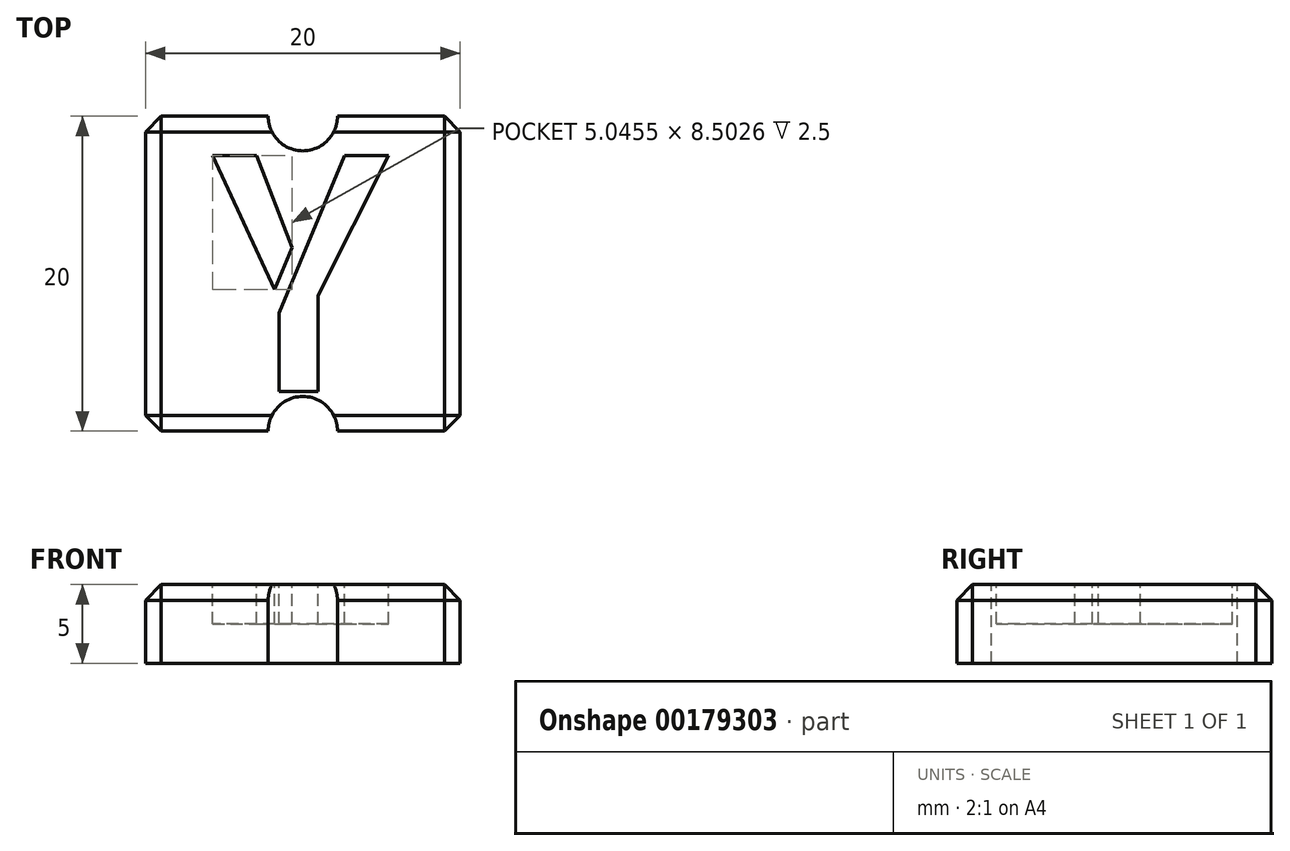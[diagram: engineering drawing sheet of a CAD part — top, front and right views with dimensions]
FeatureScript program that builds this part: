
annotation { "Feature Type Name" : "Feature", "Feature Type Description" : "" }
export const myFeature = defineFeature(function(context is Context, id is Id, definition is map)
    precondition{}
    {
        {
            var Q0;
            Q0=qCreatedBy(makeId("Top.planeOp"),FACE);
            var sketch = newSketch(context, id + "F0", { "sketchPlane" : qUnion([Q0])});
            skLineSegment(sketch, "E0.bottom", {"start": v(10, 8.66) * mm, "end": v(-10, 8.66) * mm});
            skLineSegment(sketch, "E0.top", {"start": v(10, -11.34) * mm, "end": v(-10, -11.34) * mm});
            skLineSegment(sketch, "E0.left", {"start": v(10, 8.66) * mm, "end": v(10, -11.34) * mm});
            skLineSegment(sketch, "E0.right", {"start": v(-10, 8.66) * mm, "end": v(-10, -11.34) * mm});
            skPoint(sketch, "E0.middle", {"position": v(0, -1.34) * mm});
            skArc(sketch, "E1", {"start": v(0, 12.66) * mm, "mid": v(2.83, 11.5) * mm, "end": v(4, 8.66) * mm});
            skPoint(sketch, "E1.startSnap0", {"position": v(0, 8.66) * mm});
            skArc(sketch, "E2", {"start": v(0, 12.66) * mm, "mid": v(-2.83, 11.5) * mm, "end": v(-4, 8.66) * mm});
            skArc(sketch, "E3", {"start": v(0, -15.34) * mm, "mid": v(-2.83, -14.17) * mm, "end": v(-4, -11.34) * mm});
            skPoint(sketch, "E3.startSnap0", {"position": v(0, -11.34) * mm});
            skArc(sketch, "E4", {"start": v(0, -15.34) * mm, "mid": v(2.83, -14.17) * mm, "end": v(4, -11.34) * mm});
            skSolve(sketch);
        }
        {
            var Q0;
            Q0=makeQuery(id+"F0.imprint","IMPRINT",FACE,{"disambiguationData":[TD([[makeQuery(id+"F0.imprint","IMPRINT",EDGE,{"derivedFrom":sQuery(id+"F0.wireOp",EDGE,"E0.bottom")}),1.0]])]});
            var Q1;
            {var subQ0=sQuery(id+"F0.wireOp",EDGE,"E1");Q1=makeQuery(id+"F0.imprint","IMPRINT",FACE,{"disambiguationData":[TD([[makeQuery(id+"F0.imprint","IMPRINT",EDGE,{"derivedFrom":subQ0}),-1.0]])]});}
            var Q2;
            {var subQ0=sQuery(id+"F0.wireOp",EDGE,"E3");Q2=makeQuery(id+"F0.imprint","IMPRINT",FACE,{"disambiguationData":[TD([[makeQuery(id+"F0.imprint","IMPRINT",EDGE,{"derivedFrom":subQ0}),-1.0]])]});}
            extrude(context, id + "F1", {"entities" : qUnion([Q0, Q1, Q2]), "depth" : 5 * mm});
        }
        {
            var Q0;
            Q0=makeQuery(id+"F1.opExtrude","CAP_FACE",FACE,{"disambiguationData":[OSD([sQuery(id+"F0.wireOp",EDGE,"E0.bottom"),sQuery(id+"F0.wireOp",EDGE,"E0.top"),sQuery(id+"F0.wireOp",EDGE,"E0.left"),sQuery(id+"F0.wireOp",EDGE,"E0.right")])],"isStart":false});
            var sketch = newSketch(context, id + "F2", { "sketchPlane" : qUnion([Q0])});
            skText(sketch, "E5", { "text": "Y", "fontName": "AllertaStencil-Regular.ttf"});
            skLineSegment(sketch, "E6", {"start": v(-4, 8.66) * mm, "end": v(4, 8.66) * mm, "construction": true});
            skPoint(sketch, "E7", {"position": v(0, 8.66) * mm});
            skLineSegment(sketch, "E8", {"start": v(-4, -11.34) * mm, "end": v(4, -11.34) * mm, "construction": true});
            skPoint(sketch, "E9", {"position": v(0, -11.34) * mm});
            const initialGuessF2  = {"E5": [-0.00683, -0.00884, 1, 0, 0.015]};
            skSetInitialGuess(sketch, initialGuessF2);
            skSolve(sketch);
        }
        {
            var Q0;
            Q0=makeQuery(id+"F2.imprint","IMPRINT",FACE,{"disambiguationData":[TD([[makeQuery(id+"F2.imprint","IMPRINT",EDGE,{"derivedFrom":sQuery(id+"F2.wireOp",EDGE,"E5.sketch_text.stroke-7")}),-1.0]])]});
            var Q1;
            Q1=makeQuery(id+"F2.imprint","IMPRINT",FACE,{"disambiguationData":[TD([[makeQuery(id+"F2.imprint","IMPRINT",EDGE,{"derivedFrom":sQuery(id+"F2.wireOp",EDGE,"E5.sketch_text.stroke-0")}),-1.0]])]});
            extrude(context, id + "F3", {"entities" : qUnion([Q0, Q1]), "operationType" : NewBodyOperationType.REMOVE, "oppositeDirection" : true, "depth" : 2.5 * mm});
        }
        {
            var Q0;
            Q0=sQuery(id+"F2.wireOp",VERTEX,"E7");
            var Q1;
            Q1=makeQuery(id+"F1.opExtrude","SWEPT_BODY",BODY,{"disambiguationData":[OSD([sQuery(id+"F0.wireOp",EDGE,"E0.bottom"),sQuery(id+"F0.wireOp",EDGE,"E0.top"),sQuery(id+"F0.wireOp",EDGE,"E0.left"),sQuery(id+"F0.wireOp",EDGE,"E0.right"),sQuery(id+"F0.wireOp",EDGE,"E1"),sQuery(id+"F0.wireOp",EDGE,"E2")])]});
            hole(context, id + "F4", {"style" : HoleStyle.SIMPLE, "endStyle" : HoleEndStyle.BLIND, "standardTappedOrClearance" : lookupTablePath({ "standard" : "ISO", "fit" : "Normal", "size" : "M4", "type" : "Clearance" }), "standardBlindInLast" : lookupTablePath({ "fit" : "Standard", "standard" : "ISO", "size" : "M4", "type" : "Clearance" }), "holeDiameter" : 4.4 * mm, "holeDepth" : 25 * mm, "locations" : qUnion([Q0]), "scope" : qUnion([Q1])});
        }
        {
            var Q0;
            Q0=sQuery(id+"F2.wireOp",VERTEX,"E9");
            var Q1;
            Q1=makeQuery(id+"F1.opExtrude","SWEPT_BODY",BODY,{"disambiguationData":[OSD([sQuery(id+"F0.wireOp",EDGE,"E0.bottom"),sQuery(id+"F0.wireOp",EDGE,"E0.top"),sQuery(id+"F0.wireOp",EDGE,"E0.left"),sQuery(id+"F0.wireOp",EDGE,"E0.right"),sQuery(id+"F0.wireOp",EDGE,"E1"),sQuery(id+"F0.wireOp",EDGE,"E2"),sQuery(id+"F0.wireOp",EDGE,"E3"),sQuery(id+"F0.wireOp",EDGE,"E4")])]});
            hole(context, id + "F5", {"style" : HoleStyle.SIMPLE, "endStyle" : HoleEndStyle.BLIND, "standardTappedOrClearance" : lookupTablePath({ "standard" : "ISO", "fit" : "Normal", "size" : "M4", "type" : "Clearance" }), "standardBlindInLast" : lookupTablePath({ "fit" : "Standard", "standard" : "ISO", "size" : "M4", "type" : "Clearance" }), "holeDiameter" : 4.4 * mm, "holeDepth" : 25 * mm, "locations" : qUnion([Q0]), "scope" : qUnion([Q1])});
        }
        {
            var Q0;
            Q0=makeQuery(id+"F1.opExtrude","SWEPT_EDGE",EDGE,{"disambiguationData":[OSD([sQuery(id+"F0.wireOp",EDGE,"E0.bottom"),sQuery(id+"F0.wireOp",EDGE,"E0.left")])]});
            var Q1;
            Q1=makeQuery(id+"F1.opExtrude","SWEPT_EDGE",EDGE,{"disambiguationData":[OSD([sQuery(id+"F0.wireOp",EDGE,"E0.top"),sQuery(id+"F0.wireOp",EDGE,"E0.left")])]});
            var Q2;
            Q2=makeQuery(id+"F1.opExtrude","SWEPT_EDGE",EDGE,{"disambiguationData":[OSD([sQuery(id+"F0.wireOp",EDGE,"E0.top"),sQuery(id+"F0.wireOp",EDGE,"E0.right")])]});
            var Q3;
            Q3=makeQuery(id+"F1.opExtrude","SWEPT_EDGE",EDGE,{"disambiguationData":[OSD([sQuery(id+"F0.wireOp",EDGE,"E0.bottom"),sQuery(id+"F0.wireOp",EDGE,"E0.right")])]});
            var Q4;
            Q4=makeQuery(id+"F1.opExtrude","CAP_EDGE",EDGE,{"disambiguationData":[OSD([sQuery(id+"F0.wireOp",EDGE,"E0.left")])],"isStart":false});
            var Q5;
            Q5=makeQuery(id+"F1.opExtrude","CAP_EDGE",EDGE,{"disambiguationData":[OSD([sQuery(id+"F0.wireOp",EDGE,"E0.right")])],"isStart":false});
            var Q6;
            {var subQ0=sQuery(id+"F0.wireOp",EDGE,"E0.bottom");Q6=makeQuery(id+"F1.opExtrude","CAP_EDGE",EDGE,{"disambiguationData":[OSD([subQ0]),TDD([makeQuery(id+"F0.imprint","IMPRINT",EDGE,{"disambiguationData":[TD([[makeQuery(id+"F0.imprint","INTERSECT",VERTEX,{"derivedFrom":[subQ0,sQuery(id+"F0.wireOp",EDGE,"E0.left")]}),-1.0]])],"derivedFrom":subQ0})])],"isStart":false});}
            var Q7;
            {var subQ0=sQuery(id+"F0.wireOp",EDGE,"E0.bottom");Q7=makeQuery(id+"F1.opExtrude","CAP_EDGE",EDGE,{"disambiguationData":[OSD([subQ0]),TDD([makeQuery(id+"F0.imprint","IMPRINT",EDGE,{"disambiguationData":[TD([[makeQuery(id+"F0.imprint","INTERSECT",VERTEX,{"derivedFrom":[subQ0,sQuery(id+"F0.wireOp",EDGE,"E0.right")]}),1.0]])],"derivedFrom":subQ0})])],"isStart":false});}
            var Q8;
            {var subQ0=sQuery(id+"F0.wireOp",EDGE,"E0.top");Q8=makeQuery(id+"F1.opExtrude","CAP_EDGE",EDGE,{"disambiguationData":[OSD([subQ0]),TDD([makeQuery(id+"F0.imprint","IMPRINT",EDGE,{"disambiguationData":[TD([[makeQuery(id+"F0.imprint","INTERSECT",VERTEX,{"derivedFrom":[subQ0,sQuery(id+"F0.wireOp",EDGE,"E0.left")]}),-1.0]])],"derivedFrom":subQ0})])],"isStart":false});}
            var Q9;
            {var subQ0=sQuery(id+"F0.wireOp",EDGE,"E0.top");Q9=makeQuery(id+"F1.opExtrude","CAP_EDGE",EDGE,{"disambiguationData":[OSD([subQ0]),TDD([makeQuery(id+"F0.imprint","IMPRINT",EDGE,{"disambiguationData":[TD([[makeQuery(id+"F0.imprint","INTERSECT",VERTEX,{"derivedFrom":[subQ0,sQuery(id+"F0.wireOp",EDGE,"E0.right")]}),1.0]])],"derivedFrom":subQ0})])],"isStart":false});}
            chamfer(context, id + "F6", {"entities" : qUnion([Q0, Q1, Q2, Q3, Q4, Q5, Q6, Q7, Q8, Q9]), "width" : 1 * mm, "tangentPropagation" : true});
        }
    });
